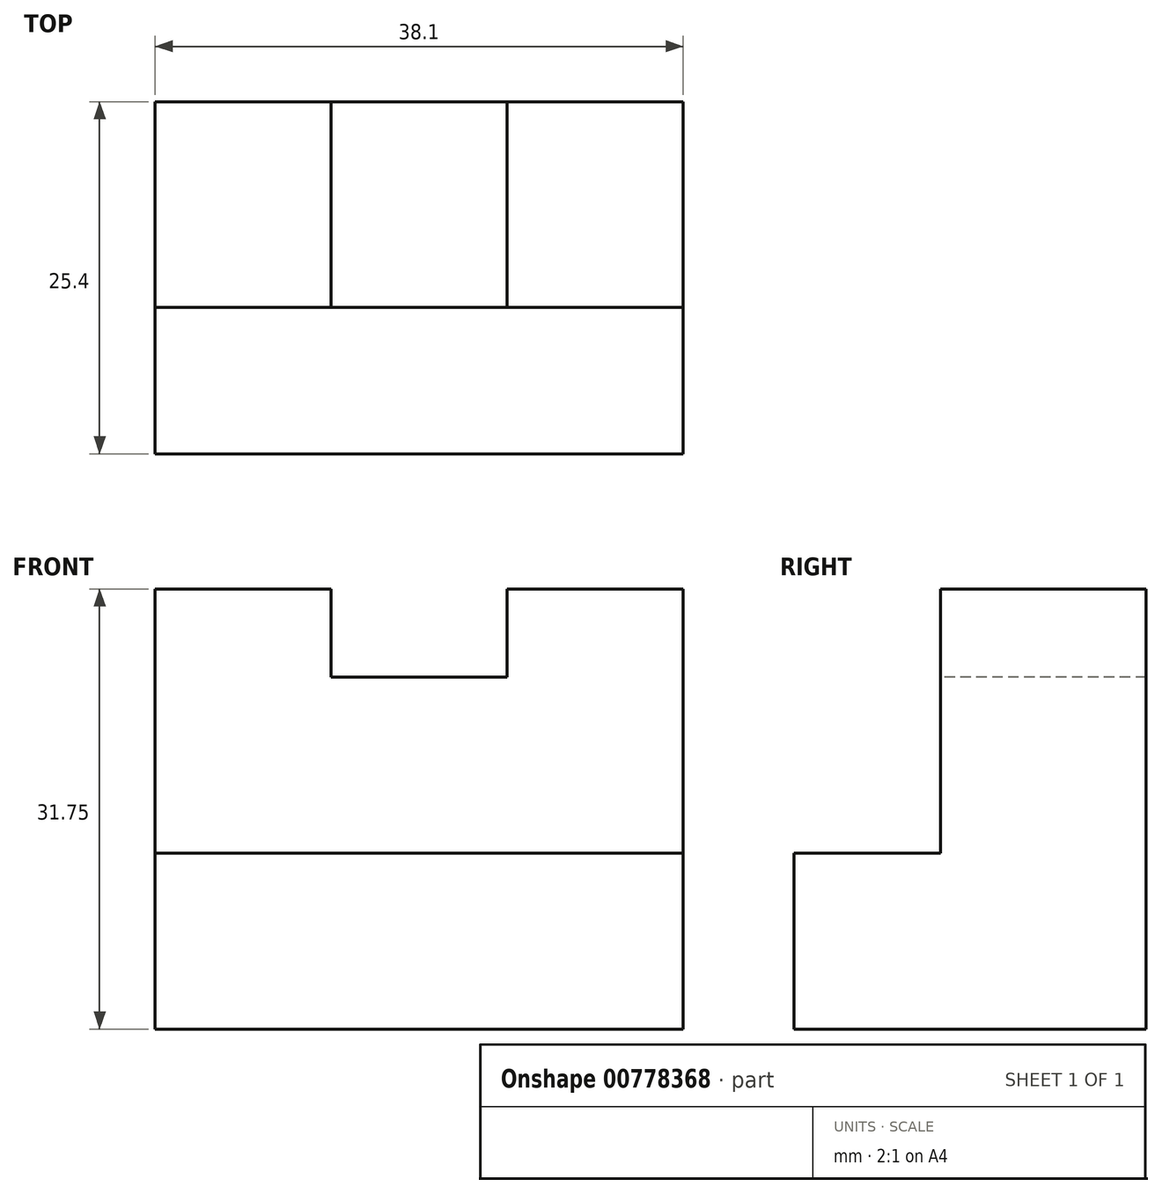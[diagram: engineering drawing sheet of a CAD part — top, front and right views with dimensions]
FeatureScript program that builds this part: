
annotation { "Feature Type Name" : "Feature", "Feature Type Description" : "" }
export const myFeature = defineFeature(function(context is Context, id is Id, definition is map)
    precondition{}
    {
        {
            var Q0;
            Q0=qCreatedBy(makeId("Front.planeOp"),FACE);
            var sketch = newSketch(context, id + "F0", { "sketchPlane" : qUnion([Q0])});
            skLineSegment(sketch, "E0", {"start": v(0, 0) * mm, "end": v(0, 31.75) * mm});
            skLineSegment(sketch, "E1", {"start": v(38.1, 0) * mm, "end": v(0, 0) * mm});
            skLineSegment(sketch, "E2", {"start": v(38.1, 0) * mm, "end": v(38.1, 31.75) * mm});
            skLineSegment(sketch, "E3", {"start": v(0, 31.75) * mm, "end": v(38.1, 31.75) * mm});
            skSolve(sketch);
        }
        {
            var Q0;
            Q0 = qSketchRegion(id + "F0", true);
            extrude(context, id + "F1", {"entities" : qUnion([Q0]), "depth" : 25.4 * mm, "offsetDistance" : 25.4 * mm});
        }
        {
            var Q0;
            Q0=makeQuery(id+"F1.opExtrude","SWEPT_FACE",FACE,{"disambiguationData":[OSD([sQuery(id+"F0.wireOp",EDGE,"E2")])]});
            var sketch = newSketch(context, id + "F2", { "sketchPlane" : qUnion([Q0])});
            skLineSegment(sketch, "E4", {"start": v(0, 31.75) * mm, "end": v(0, 0) * mm});
            skLineSegment(sketch, "E5", {"start": v(0, 0) * mm, "end": v(-25.4, 0) * mm});
            skLineSegment(sketch, "E6", {"start": v(-25.4, 0) * mm, "end": v(0, 0) * mm});
            skLineSegment(sketch, "E7", {"start": v(-25.4, 12.7) * mm, "end": v(-25.4, 0) * mm});
            skLineSegment(sketch, "E8", {"start": v(-14.83, 12.7) * mm, "end": v(-25.4, 12.7) * mm});
            skLineSegment(sketch, "E9", {"start": v(-14.83, 12.7) * mm, "end": v(-14.83, 31.75) * mm});
            skSolve(sketch);
        }
        {
            var Q0;
            {var subQ0=sQuery(id+"F2.wireOp",EDGE,"E8");Q0=makeQuery(id+"F2.imprint","IMPRINT",FACE,{"disambiguationData":[TD([[makeQuery(id+"F2.imprint","IMPRINT",EDGE,{"derivedFrom":subQ0}),-1.0]])]});}
            extrude(context, id + "F3", {"entities" : qUnion([Q0]), "operationType" : NewBodyOperationType.REMOVE, "oppositeDirection" : true, "depth" : 38.1 * mm, "offsetDistance" : 25.4 * mm});
        }
        {
            var Q0;
            Q0=makeQuery(id+"F3.boolean.opBoolean","COPY",FACE,{"derivedFrom":makeQuery(id+"F3.opExtrude","SWEPT_FACE",FACE,{"disambiguationData":[OSD([sQuery(id+"F2.wireOp",EDGE,"E9")])]})});
            var sketch = newSketch(context, id + "F4", { "sketchPlane" : qUnion([Q0])});
            skLineSegment(sketch, "E10", {"start": v(12.7, 31.75) * mm, "end": v(0, 31.75) * mm});
            skLineSegment(sketch, "E11", {"start": v(12.7, 25.4) * mm, "end": v(12.7, 31.75) * mm});
            skLineSegment(sketch, "E12", {"start": v(25.4, 25.4) * mm, "end": v(12.7, 25.4) * mm});
            skLineSegment(sketch, "E13", {"start": v(25.4, 25.4) * mm, "end": v(25.4, 31.75) * mm});
            skLineSegment(sketch, "E14", {"start": v(25.4, 31.75) * mm, "end": v(38.1, 31.75) * mm});
            skSolve(sketch);
        }
        {
            var Q0;
            {var subQ0=sQuery(id+"F4.wireOp",EDGE,"E11");Q0=makeQuery(id+"F4.imprint","IMPRINT",FACE,{"disambiguationData":[TD([[makeQuery(id+"F4.imprint","IMPRINT",EDGE,{"derivedFrom":subQ0}),-1.0]])]});}
            extrude(context, id + "F5", {"entities" : qUnion([Q0]), "operationType" : NewBodyOperationType.REMOVE, "oppositeDirection" : true, "depth" : 25.4 * mm, "offsetDistance" : 25.4 * mm});
        }
    });
